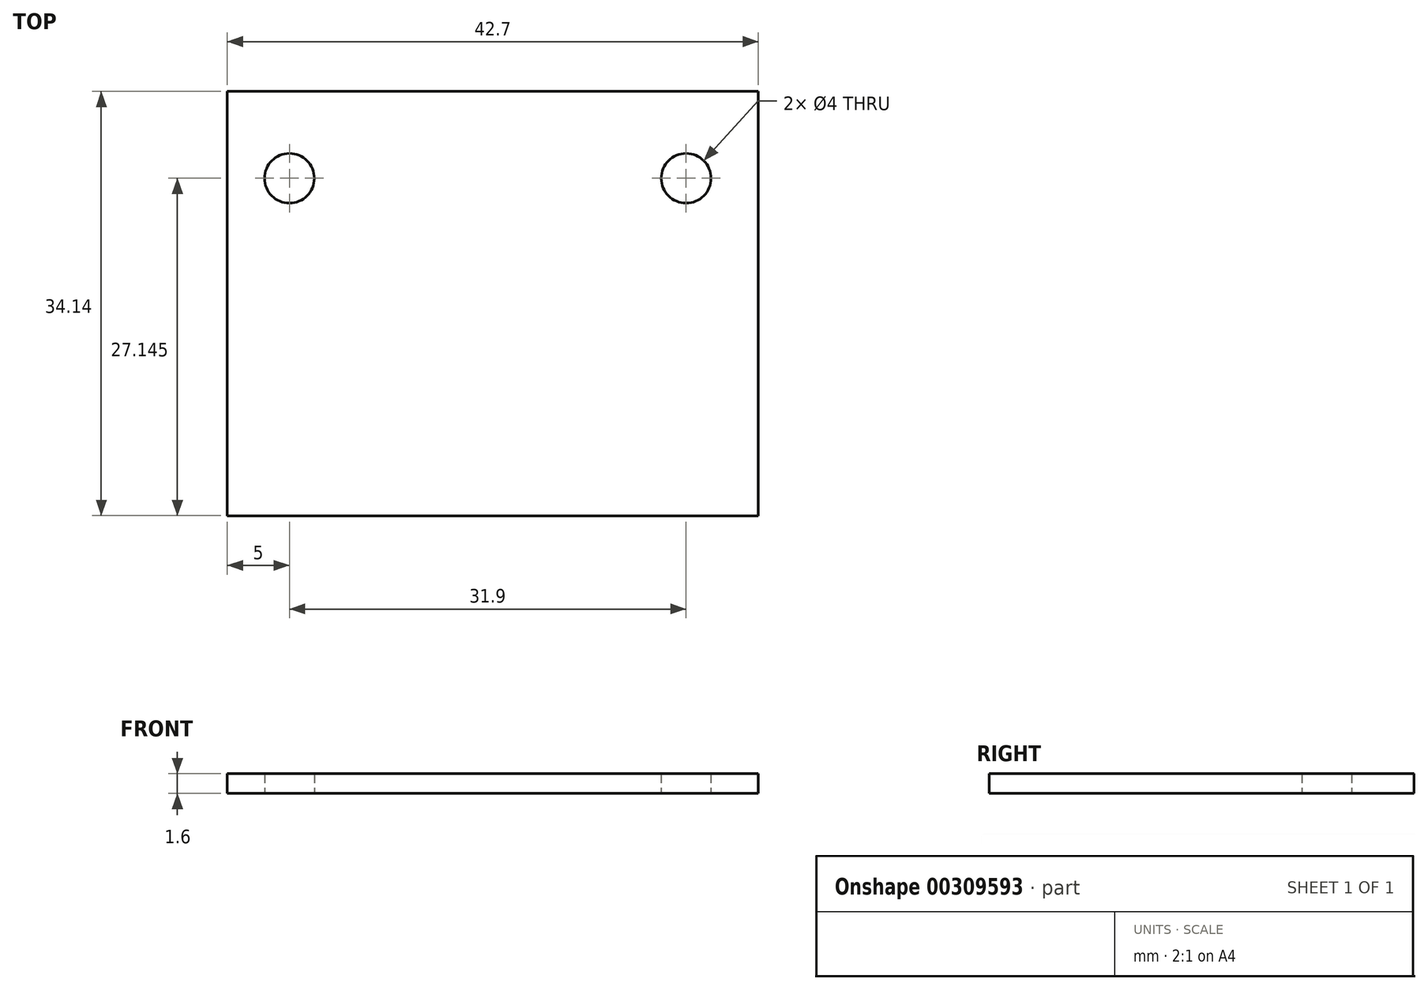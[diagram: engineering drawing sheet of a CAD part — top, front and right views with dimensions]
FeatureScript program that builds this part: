
annotation { "Feature Type Name" : "Feature", "Feature Type Description" : "" }
export const myFeature = defineFeature(function(context is Context, id is Id, definition is map)
    precondition{}
    {
        {
            assignVariable(context, id + "F0", {"name" : "PCB_THICKNESS", "anyValue" : 1.6});
        }
        {
            assignVariable(context, id + "F1", {"name" : "HOLE_DIA", "anyValue" : 4});
        }
        {
            var Q0;
            Q0=qCreatedBy(makeId("Top.planeOp"),FACE);
            var sketch = newSketch(context, id + "F2", { "sketchPlane" : qUnion([Q0])});
            skLineSegment(sketch, "E0.bottom", {"start": v(-21.35, 17.07) * mm, "end": v(21.35, 17.07) * mm});
            skLineSegment(sketch, "E0.top", {"start": v(-21.35, -17.08) * mm, "end": v(21.35, -17.08) * mm});
            skLineSegment(sketch, "E0.left", {"start": v(-21.35, 17.07) * mm, "end": v(-21.35, -17.08) * mm});
            skLineSegment(sketch, "E0.right", {"start": v(21.35, 17.07) * mm, "end": v(21.35, -17.08) * mm});
            skPoint(sketch, "E0.middle", {"position": v(0, 0) * mm});
            skPoint(sketch, "E1", {"position": v(-16.35, 10.08) * mm});
            skPoint(sketch, "E2", {"position": v(15.55, 10.08) * mm});
            skSolve(sketch);
        }
        {
            var Q0;
            Q0=makeQuery(id+"F2.imprint","IMPRINT",FACE,{"disambiguationData":[TD([[makeQuery(id+"F2.imprint","IMPRINT",EDGE,{"derivedFrom":sQuery(id+"F2.wireOp",EDGE,"E0.bottom")}),-1.0]])]});
            extrude(context, id + "F3", {"entities" : qUnion([Q0]), "depth" : (getVariable(context, 'PCB_THICKNESS')) * mm, "offsetDistance" : 25 * mm});
        }
        {
            var Q0;
            Q0=sQuery(id+"F2.wireOp",VERTEX,"E1");
            var Q1;
            Q1=sQuery(id+"F2.wireOp",VERTEX,"E2");
            var Q2;
            Q2=makeQuery(id+"F3.opExtrude","SWEPT_BODY",BODY,{"disambiguationData":[OSD([sQuery(id+"F2.wireOp",EDGE,"E0.bottom"),sQuery(id+"F2.wireOp",EDGE,"E0.top"),sQuery(id+"F2.wireOp",EDGE,"E0.left"),sQuery(id+"F2.wireOp",EDGE,"E0.right")])]});
            hole(context, id + "F4", {"style" : HoleStyle.SIMPLE, "endStyle" : HoleEndStyle.THROUGH, "oppositeDirection" : true, "holeDiameter" : (getVariable(context, 'HOLE_DIA')) * mm, "majorDiameter" : 5 * mm, "isTappedThrough" : true, "tappedDepth" : 12 * mm, "tapClearance" : 3, "startFromSketch" : true, "locations" : qUnion([Q0, Q1]), "scope" : qUnion([Q2])});
        }
    });
